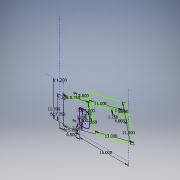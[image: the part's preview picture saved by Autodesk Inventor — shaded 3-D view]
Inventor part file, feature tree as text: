
AUTODESK INVENTOR PART (.ipt)
format: ipt  version: 2017 SP1 (Build 210196100, 196)  size: 124,928 bytes
history: native  units: in
note: dims shown in document units (in); Inventor stores cm internally (conversion verified against a paired STEP export)
features: sketch x1
ambient origin geometry x8: Origin, YZ Plane, XZ Plane, XY Plane, X Axis, Y Axis, Z Axis, Center Point
feature tree (1):
  sketch  "Sketch1"  dims[d0=2.5in d1=5.0in d2=1.25in d3=0.75in d4=16.0in d7=5.0in d8=8.0in d9=5.0in d10=8.75in d11=0.25in d12=13.0in d13=11.0in d14=3.0in d17=3.5in d19=2.0in d20=11.0in d22=1.25in d23=4.0in d24=1.0in d25=6.5in d30=1.0in d31=4.5in d34=11.5in d36=1.0in d38=1.2in d39=1.0in d41=6.5in d42=5.0in d43=0.25in d44=7.75in d45=5.25in]
